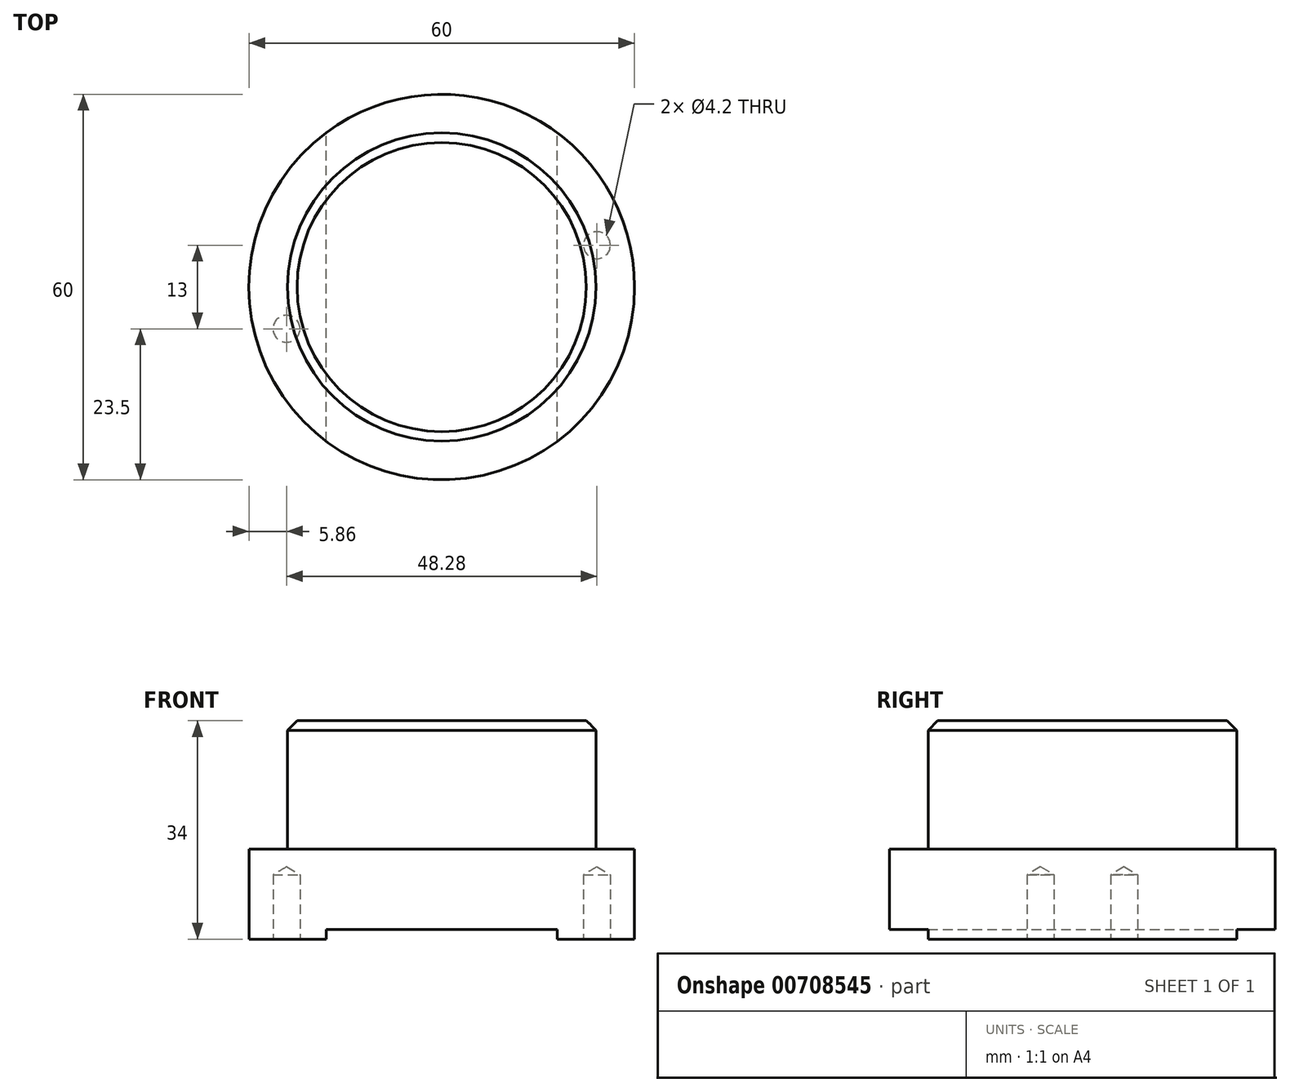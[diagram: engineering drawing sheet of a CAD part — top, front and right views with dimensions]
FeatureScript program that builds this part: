
annotation { "Feature Type Name" : "Feature", "Feature Type Description" : "" }
export const myFeature = defineFeature(function(context is Context, id is Id, definition is map)
    precondition{}
    {
        {
            var Q0;
            Q0=qCreatedBy(makeId("Top.planeOp"),FACE);
            var sketch = newSketch(context, id + "F0", { "sketchPlane" : qUnion([Q0])});
            skCircle(sketch, "E0", {"center": v(0, 0) * mm, "radius": 30 * mm});
            skSolve(sketch);
        }
        {
            var Q0;
            Q0=makeQuery(id+"F0.imprint","IMPRINT",FACE,{"disambiguationData":[TD([[makeQuery(id+"F0.imprint","IMPRINT",EDGE,{"derivedFrom":sQuery(id+"F0.wireOp",EDGE,"E0")}),1.0]])]});
            extrude(context, id + "F1", {"entities" : qUnion([Q0]), "depth" : 14 * mm, "offsetDistance" : 25 * mm});
        }
        {
            var Q0;
            Q0=makeQuery(id+"F1.opExtrude","CAP_FACE",FACE,{"disambiguationData":[OSD([sQuery(id+"F0.wireOp",EDGE,"E0")])],"isStart":false});
            var sketch = newSketch(context, id + "F2", { "sketchPlane" : qUnion([Q0])});
            skCircle(sketch, "E1", {"center": v(0, 0) * mm, "radius": 24 * mm});
            skSolve(sketch);
        }
        {
            var Q0;
            Q0=makeQuery(id+"F2.imprint","IMPRINT",FACE,{"disambiguationData":[TD([[makeQuery(id+"F2.imprint","IMPRINT",EDGE,{"derivedFrom":sQuery(id+"F2.wireOp",EDGE,"E1")}),1.0]])]});
            extrude(context, id + "F3", {"entities" : qUnion([Q0]), "operationType" : NewBodyOperationType.ADD, "depth" : 20 * mm, "offsetDistance" : 25 * mm});
        }
        {
            var Q0;
            Q0=makeQuery(id+"F3.opExtrude","CAP_EDGE",EDGE,{"disambiguationData":[OSD([sQuery(id+"F2.wireOp",EDGE,"E1")])],"isStart":false});
            chamfer(context, id + "F4", {"entities" : qUnion([Q0]), "width" : 1.5 * mm, "tangentPropagation" : true});
        }
        {
            var Q0;
            Q0=makeQuery(id+"F1.opExtrude","CAP_FACE",FACE,{"disambiguationData":[OSD([sQuery(id+"F0.wireOp",EDGE,"E0")])],"isStart":true});
            var sketch = newSketch(context, id + "F5", { "sketchPlane" : qUnion([Q0])});
            skLineSegment(sketch, "E2.bottom", {"start": v(-18, 36.33) * mm, "end": v(18, 36.33) * mm});
            skLineSegment(sketch, "E2.top", {"start": v(-18, -38.87) * mm, "end": v(18, -38.87) * mm});
            skLineSegment(sketch, "E2.left", {"start": v(-18, 36.33) * mm, "end": v(-18, -38.87) * mm});
            skLineSegment(sketch, "E2.right", {"start": v(18, 36.33) * mm, "end": v(18, -38.87) * mm});
            skSolve(sketch);
        }
        {
            var Q0;
            {var subQ0=sQuery(id+"F5.wireOp",EDGE,"E2.bottom");Q0=makeQuery(id+"F5.imprint","IMPRINT",FACE,{"disambiguationData":[TD([[makeQuery(id+"F5.imprint","IMPRINT",EDGE,{"derivedFrom":subQ0}),-1.0]])]});}
            var Q1;
            {var subQ0=sQuery(id+"F5.wireOp",EDGE,"E2.left");var subQ1=makeQuery(id+"F1.opExtrude","CAP_EDGE",EDGE,{"disambiguationData":[OSD([sQuery(id+"F0.wireOp",EDGE,"E0")])],"isStart":true});var subQ2=makeQuery(id+"F5.imprint","INTERSECT",VERTEX,{"disambiguationData":[OD(0.0)],"derivedFrom":[subQ1,subQ0]});Q1=makeQuery(id+"F5.imprint","IMPRINT",FACE,{"disambiguationData":[TD([[makeQuery(id+"F5.imprint","IMPRINT",EDGE,{"disambiguationData":[TD([[subQ2,-1.0]])],"derivedFrom":subQ0}),1.0]])]});}
            var Q2;
            {var subQ0=sQuery(id+"F5.wireOp",EDGE,"E2.top");Q2=makeQuery(id+"F5.imprint","IMPRINT",FACE,{"disambiguationData":[TD([[makeQuery(id+"F5.imprint","IMPRINT",EDGE,{"derivedFrom":subQ0}),1.0]])]});}
            extrude(context, id + "F6", {"entities" : qUnion([Q0, Q1, Q2]), "operationType" : NewBodyOperationType.REMOVE, "oppositeDirection" : true, "depth" : 1.5 * mm, "offsetDistance" : 25 * mm});
        }
        {
            var Q0;
            {var subQ0=sQuery(id+"F0.wireOp",EDGE,"E0");Q0=makeQuery(id+"F6.boolean.opBoolean","SPLIT",FACE,{"disambiguationData":[TD([makeQuery(id+"F6.opExtrude","SWEPT_FACE",FACE,{"disambiguationData":[OSD([sQuery(id+"F5.wireOp",EDGE,"E2.left")])]})])],"derivedFrom":makeQuery(id+"F1.opExtrude","CAP_FACE",FACE,{"disambiguationData":[OSD([subQ0])],"isStart":true})});}
            var sketch = newSketch(context, id + "F7", { "sketchPlane" : qUnion([Q0])});
            skPoint(sketch, "E3", {"position": v(-24.14, 6.5) * mm});
            skPoint(sketch, "E4", {"position": v(24.14, -6.5) * mm});
            skSolve(sketch);
        }
        {
            var Q0;
            Q0=sQuery(id+"F7.wireOp",VERTEX,"E3");
            var Q1;
            Q1=sQuery(id+"F7.wireOp",VERTEX,"E4");
            var Q2;
            Q2=makeQuery(id+"F1.opExtrude","SWEPT_BODY",BODY,{"disambiguationData":[OSD([sQuery(id+"F0.wireOp",EDGE,"E0")])]});
            hole(context, id + "F8", {"style" : HoleStyle.SIMPLE, "endStyle" : HoleEndStyle.BLIND, "standardTappedOrClearance" : lookupTablePath({ "standard" : "ISO", "fit" : "Close", "size" : "M4", "type" : "Clearance" }), "standardBlindInLast" : lookupTablePath({ "fit" : "Close", "standard" : "ISO", "size" : "M4", "type" : "Clearance" }), "holeDiameter" : 4.2 * mm, "majorDiameter" : 5 * mm, "holeDepth" : 10 * mm, "isTappedThrough" : true, "tappedDepth" : 12 * mm, "tapClearance" : 3, "locations" : qUnion([Q0, Q1]), "scope" : qUnion([Q2])});
        }
    });
